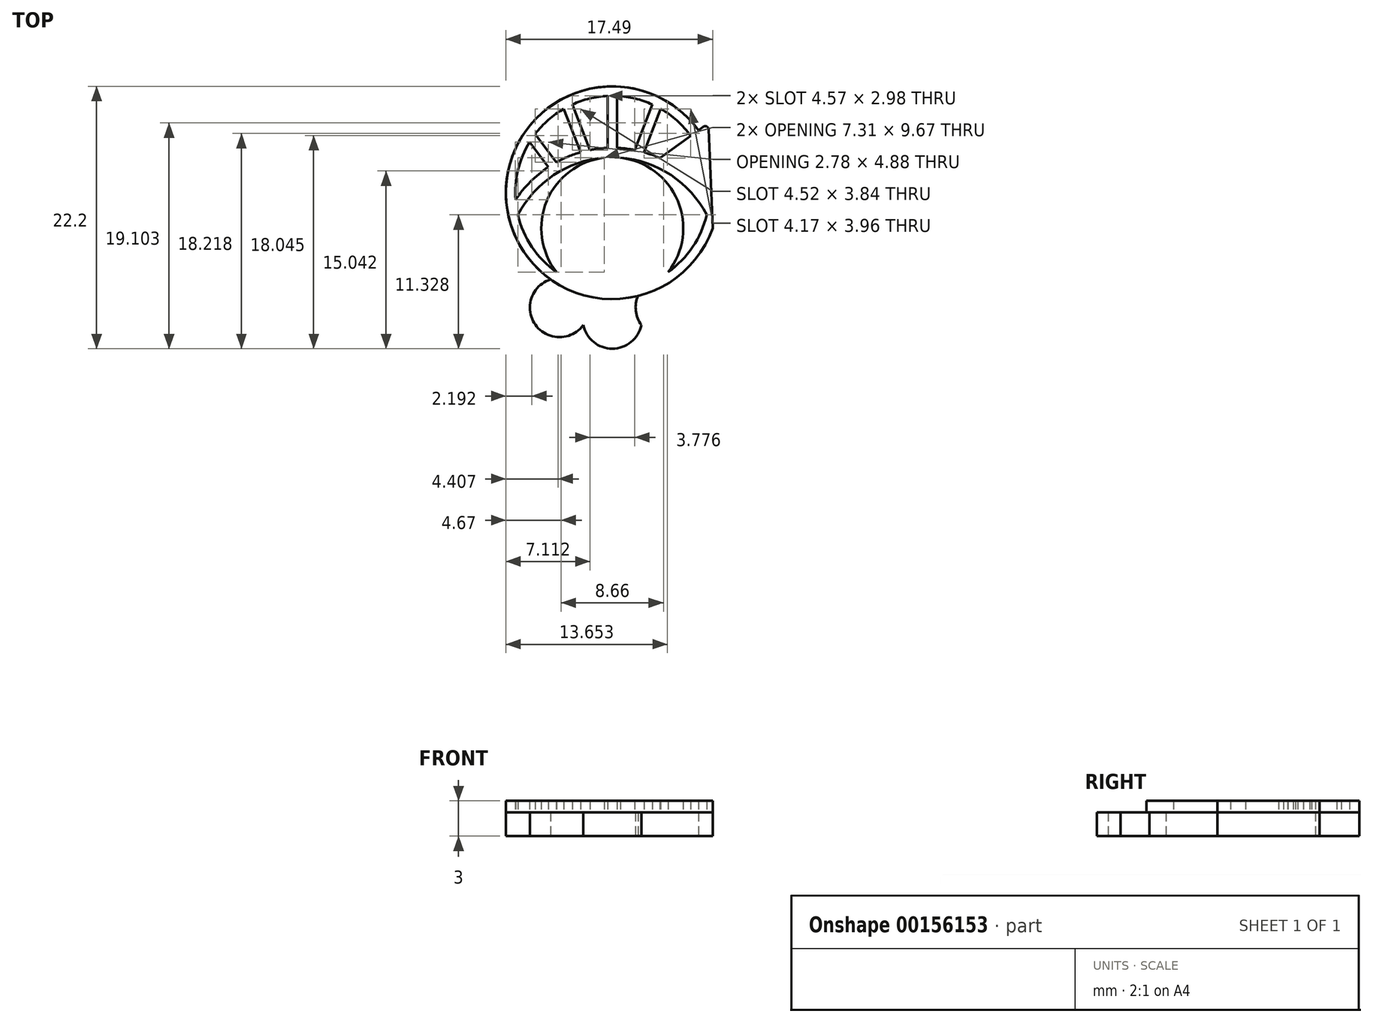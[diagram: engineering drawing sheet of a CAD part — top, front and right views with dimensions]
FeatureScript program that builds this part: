
annotation { "Feature Type Name" : "Feature", "Feature Type Description" : "" }
export const myFeature = defineFeature(function(context is Context, id is Id, definition is map)
    precondition{}
    {
        {
            var Q0;
            Q0=qCreatedBy(makeId("Top.planeOp"),FACE);
            var sketch = newSketch(context, id + "F0", { "sketchPlane" : qUnion([Q0])});
            skCircle(sketch, "E0", {"center": v(0, 0) * mm, "radius": 9 * mm});
            skLineSegment(sketch, "E1", {"start": v(0, -9) * mm, "end": v(0, -3) * mm, "construction": true});
            skLineSegment(sketch, "E2", {"start": v(-11.27, -3) * mm, "end": v(11.18, -3) * mm, "construction": true});
            skLineSegment(sketch, "E3", {"start": v(8.14, 5.36) * mm, "end": v(8.49, -3) * mm});
            skLineSegment(sketch, "E4", {"start": v(7.69, 5.58) * mm, "end": v(4.03, 2.93) * mm});
            skPoint(sketch, "E5.visualSharp", {"position": v(8.12, 5.9) * mm});
            skArc(sketch, "E5.filletArc", {"start": v(8.14, 5.36) * mm, "mid": v(7.98, 5.6) * mm, "end": v(7.69, 5.58) * mm});
            skCircle(sketch, "E6.0", {"center": v(0, 0) * mm, "radius": 8.2 * mm});
            skLineSegment(sketch, "E7", {"start": v(-7.53, 0.27) * mm, "end": v(-8.15, 0.95) * mm});
            skLineSegment(sketch, "E8", {"start": v(-7, 0.87) * mm, "end": v(-7.97, 1.94) * mm});
            skLineSegment(sketch, "E9", {"start": v(-5.42, 2.17) * mm, "end": v(-7, 4.28) * mm});
            skLineSegment(sketch, "E10", {"start": v(-4.73, 2.58) * mm, "end": v(-6.51, 4.98) * mm});
            skLineSegment(sketch, "E11", {"start": v(-2.67, 3.43) * mm, "end": v(-4.1, 7.1) * mm});
            skLineSegment(sketch, "E12", {"start": v(-1.89, 3.62) * mm, "end": v(-3.38, 7.47) * mm});
            skLineSegment(sketch, "E13", {"start": v(-0.4, 8.2) * mm, "end": v(-0.4, 3.8) * mm});
            skLineSegment(sketch, "E14", {"start": v(0.4, 8.2) * mm, "end": v(0.4, 3.8) * mm});
            skLineSegment(sketch, "E15", {"start": v(1.89, 3.62) * mm, "end": v(3.38, 7.47) * mm});
            skLineSegment(sketch, "E16", {"start": v(2.67, 3.43) * mm, "end": v(4.1, 7.1) * mm});
            skArc(sketch, "E17", {"start": v(8.18, -0.6) * mm, "mid": v(0, 3.8) * mm, "end": v(-8.18, -0.6) * mm});
            skArc(sketch, "E18", {"start": v(7.98, -1.87) * mm, "mid": v(0, 2.99) * mm, "end": v(-7.98, -1.87) * mm});
            skArc(sketch, "E19", {"start": v(-5.22, -7.33) * mm, "mid": v(-6.5, -11.18) * mm, "end": v(-2.45, -11.2) * mm});
            skArc(sketch, "E20", {"start": v(-2.02, -9.23) * mm, "mid": v(-2.08, -8.98) * mm, "end": v(-2.17, -8.73) * mm});
            skArc(sketch, "E21", {"start": v(-2.45, -11.2) * mm, "mid": v(-2.03, -10.26) * mm, "end": v(-2.02, -9.23) * mm});
            skArc(sketch, "E22", {"start": v(4.72, -6.7) * mm, "mid": v(5.48, -0.56) * mm, "end": v(0.4, 2.99) * mm});
            skArc(sketch, "E23", {"start": v(-1.67, -8.84) * mm, "mid": v(0, -13.2) * mm, "end": v(1.67, -8.84) * mm});
            skArc(sketch, "E24", {"start": v(5.22, -7.33) * mm, "mid": v(5.52, -12) * mm, "end": v(2.17, -8.73) * mm});
            skArc(sketch, "E25", {"start": v(-0.68, 2.96) * mm, "mid": v(-5.54, -0.69) * mm, "end": v(-4.72, -6.7) * mm});
            skSolve(sketch);
        }
        {
            var Q0;
            {var subQ0=sQuery(id+"F0.wireOp",EDGE,"E9");Q0=makeQuery(id+"F0.imprint","IMPRINT",FACE,{"disambiguationData":[TD([[makeQuery(id+"F0.imprint","IMPRINT",EDGE,{"derivedFrom":subQ0}),-1.0]])]});}
            var Q1;
            {var subQ0=sQuery(id+"F0.wireOp",EDGE,"E17");var subQ6=sQuery(id+"F0.wireOp",EDGE,"E6.0");var subQ14=makeQuery(id+"F0.imprint","INTERSECT",VERTEX,{"disambiguationData":[OD(1.0)],"derivedFrom":[subQ6,subQ0]});Q1=makeQuery(id+"F0.imprint","IMPRINT",FACE,{"disambiguationData":[TD([[makeQuery(id+"F0.imprint","IMPRINT",EDGE,{"disambiguationData":[TD([[subQ14,-1.0]])],"derivedFrom":subQ6}),1.0]])]});}
            var Q2;
            {var subQ0=sQuery(id+"F0.wireOp",EDGE,"E12");Q2=makeQuery(id+"F0.imprint","IMPRINT",FACE,{"disambiguationData":[TD([[makeQuery(id+"F0.imprint","IMPRINT",EDGE,{"derivedFrom":subQ0}),-1.0]])]});}
            var Q3;
            {var subQ0=sQuery(id+"F0.wireOp",EDGE,"E24");var subQ1=sQuery(id+"F0.wireOp",EDGE,"E0");var subQ2=makeQuery(id+"F0.imprint","INTERSECT",VERTEX,{"disambiguationData":[OD(0.0)],"derivedFrom":[subQ1,subQ0]});Q3=makeQuery(id+"F0.imprint","IMPRINT",FACE,{"disambiguationData":[TD([[makeQuery(id+"F0.imprint","IMPRINT",EDGE,{"disambiguationData":[TD([[subQ2,1.0]])],"derivedFrom":subQ1}),-1.0]])]});}
            var Q4;
            {var subQ0=sQuery(id+"F0.wireOp",EDGE,"E22");var subQ1=sQuery(id+"F0.wireOp",EDGE,"E6.0");var subQ2=makeQuery(id+"F0.imprint","INTERSECT",VERTEX,{"disambiguationData":[OD(0.0)],"derivedFrom":[subQ1,subQ0]});Q4=makeQuery(id+"F0.imprint","IMPRINT",FACE,{"disambiguationData":[TD([[makeQuery(id+"F0.imprint","IMPRINT",EDGE,{"disambiguationData":[TD([[subQ2,1.0]])],"derivedFrom":subQ1}),1.0]])]});}
            var Q5;
            {var subQ5=sQuery(id+"F0.wireOp",EDGE,"E16");Q5=makeQuery(id+"F0.imprint","IMPRINT",FACE,{"disambiguationData":[TD([[makeQuery(id+"F0.imprint","IMPRINT",EDGE,{"derivedFrom":subQ5}),-1.0]])]});}
            var Q6;
            {var subQ0=sQuery(id+"F0.wireOp",EDGE,"E3");var subQ1=sQuery(id+"F0.wireOp",EDGE,"E0");var subQ2=makeQuery(id+"F0.imprint","INTERSECT",VERTEX,{"disambiguationData":[OD(0.0)],"derivedFrom":[subQ1,subQ0]});Q6=makeQuery(id+"F0.imprint","IMPRINT",FACE,{"disambiguationData":[TD([[makeQuery(id+"F0.imprint","IMPRINT",EDGE,{"disambiguationData":[TD([[subQ2,-1.0]])],"derivedFrom":subQ1}),1.0]])]});}
            var Q7;
            {var subQ0=sQuery(id+"F0.wireOp",EDGE,"E11");Q7=makeQuery(id+"F0.imprint","IMPRINT",FACE,{"disambiguationData":[TD([[makeQuery(id+"F0.imprint","IMPRINT",EDGE,{"derivedFrom":subQ0}),-1.0]])]});}
            var Q8;
            {var subQ0=sQuery(id+"F0.wireOp",EDGE,"E7");Q8=makeQuery(id+"F0.imprint","IMPRINT",FACE,{"disambiguationData":[TD([[makeQuery(id+"F0.imprint","IMPRINT",EDGE,{"derivedFrom":subQ0}),-1.0]])]});}
            var Q9;
            {var subQ0=sQuery(id+"F0.wireOp",EDGE,"E19");Q9=makeQuery(id+"F0.imprint","IMPRINT",FACE,{"disambiguationData":[TD([[makeQuery(id+"F0.imprint","IMPRINT",EDGE,{"derivedFrom":subQ0}),1.0]])]});}
            var Q10;
            {var subQ0=sQuery(id+"F0.wireOp",EDGE,"E10");Q10=makeQuery(id+"F0.imprint","IMPRINT",FACE,{"disambiguationData":[TD([[makeQuery(id+"F0.imprint","IMPRINT",EDGE,{"derivedFrom":subQ0}),-1.0]])]});}
            var Q11;
            {var subQ0=sQuery(id+"F0.wireOp",EDGE,"E18");var subQ1=sQuery(id+"F0.wireOp",EDGE,"E6.0");var subQ2=makeQuery(id+"F0.imprint","INTERSECT",VERTEX,{"disambiguationData":[OD(1.0)],"derivedFrom":[subQ1,subQ0]});Q11=makeQuery(id+"F0.imprint","IMPRINT",FACE,{"disambiguationData":[TD([[makeQuery(id+"F0.imprint","IMPRINT",EDGE,{"disambiguationData":[TD([[subQ2,-1.0]])],"derivedFrom":subQ1}),1.0]])]});}
            var Q12;
            {var subQ0=sQuery(id+"F0.wireOp",EDGE,"E24");var subQ1=sQuery(id+"F0.wireOp",EDGE,"E23");var subQ2=makeQuery(id+"F0.imprint","INTERSECT",VERTEX,{"disambiguationData":[OD(0.0)],"derivedFrom":[subQ1,subQ0]});Q12=makeQuery(id+"F0.imprint","IMPRINT",FACE,{"disambiguationData":[TD([[makeQuery(id+"F0.imprint","IMPRINT",EDGE,{"disambiguationData":[TD([[subQ2,-1.0]])],"derivedFrom":subQ1}),1.0]])]});}
            var Q13;
            {var subQ0=sQuery(id+"F0.wireOp",EDGE,"E8");Q13=makeQuery(id+"F0.imprint","IMPRINT",FACE,{"disambiguationData":[TD([[makeQuery(id+"F0.imprint","IMPRINT",EDGE,{"derivedFrom":subQ0}),-1.0]])]});}
            var Q14;
            {var subQ14=sQuery(id+"F0.wireOp",EDGE,"E0");var subQ21=sQuery(id+"F0.wireOp",EDGE,"E4");var subQ27=makeQuery(id+"F0.imprint","INTERSECT",VERTEX,{"derivedFrom":[subQ14,subQ21]});Q14=makeQuery(id+"F0.imprint","IMPRINT",FACE,{"disambiguationData":[TD([[makeQuery(id+"F0.imprint","IMPRINT",EDGE,{"disambiguationData":[TD([[subQ27,1.0]])],"derivedFrom":subQ14}),1.0]])]});}
            var Q15;
            {var subQ0=sQuery(id+"F0.wireOp",EDGE,"E13");Q15=makeQuery(id+"F0.imprint","IMPRINT",FACE,{"disambiguationData":[TD([[makeQuery(id+"F0.imprint","IMPRINT",EDGE,{"derivedFrom":subQ0}),1.0]])]});}
            var Q16;
            {var subQ0=sQuery(id+"F0.wireOp",EDGE,"E7");Q16=makeQuery(id+"F0.imprint","IMPRINT",FACE,{"disambiguationData":[TD([[makeQuery(id+"F0.imprint","IMPRINT",EDGE,{"derivedFrom":subQ0}),1.0]])]});}
            var Q17;
            {var subQ0=sQuery(id+"F0.wireOp",EDGE,"E15");Q17=makeQuery(id+"F0.imprint","IMPRINT",FACE,{"disambiguationData":[TD([[makeQuery(id+"F0.imprint","IMPRINT",EDGE,{"derivedFrom":subQ0}),-1.0]])]});}
            var Q18;
            {var subQ0=sQuery(id+"F0.wireOp",EDGE,"E14");Q18=makeQuery(id+"F0.imprint","IMPRINT",FACE,{"disambiguationData":[TD([[makeQuery(id+"F0.imprint","IMPRINT",EDGE,{"derivedFrom":subQ0}),1.0]])]});}
            var Q19;
            {var subQ0=sQuery(id+"F0.wireOp",EDGE,"E21");Q19=makeQuery(id+"F0.imprint","IMPRINT",FACE,{"disambiguationData":[TD([[makeQuery(id+"F0.imprint","IMPRINT",EDGE,{"derivedFrom":subQ0}),1.0]])]});}
            var Q20;
            {var subQ0=sQuery(id+"F0.wireOp",EDGE,"E17");var subQ1=sQuery(id+"F0.wireOp",EDGE,"E4");var subQ2=makeQuery(id+"F0.imprint","INTERSECT",VERTEX,{"derivedFrom":[subQ1,subQ0]});Q20=makeQuery(id+"F0.imprint","IMPRINT",FACE,{"disambiguationData":[TD([[makeQuery(id+"F0.imprint","IMPRINT",EDGE,{"disambiguationData":[TD([[subQ2,1.0]])],"derivedFrom":subQ1}),1.0]])]});}
            var Q21;
            {var subQ1=sQuery(id+"F0.wireOp",EDGE,"E21");Q21=makeQuery(id+"F0.imprint","IMPRINT",FACE,{"disambiguationData":[TD([[makeQuery(id+"F0.imprint","IMPRINT",EDGE,{"derivedFrom":subQ1}),-1.0]])]});}
            var Q22;
            {var subQ0=sQuery(id+"F0.wireOp",EDGE,"E18");var subQ1=sQuery(id+"F0.wireOp",EDGE,"E6.0");var subQ2=makeQuery(id+"F0.imprint","INTERSECT",VERTEX,{"disambiguationData":[OD(0.0)],"derivedFrom":[subQ1,subQ0]});Q22=makeQuery(id+"F0.imprint","IMPRINT",FACE,{"disambiguationData":[TD([[makeQuery(id+"F0.imprint","IMPRINT",EDGE,{"disambiguationData":[TD([[subQ2,1.0]])],"derivedFrom":subQ1}),1.0]])]});}
            var Q23;
            {var subQ5=sQuery(id+"F0.wireOp",EDGE,"E5.filletArc");Q23=makeQuery(id+"F0.imprint","IMPRINT",FACE,{"disambiguationData":[TD([[makeQuery(id+"F0.imprint","IMPRINT",EDGE,{"derivedFrom":subQ5}),1.0]])]});}
            var Q24;
            {var subQ0=sQuery(id+"F0.wireOp",EDGE,"E20");Q24=makeQuery(id+"F0.imprint","IMPRINT",FACE,{"disambiguationData":[TD([[makeQuery(id+"F0.imprint","IMPRINT",EDGE,{"derivedFrom":subQ0}),-1.0]])]});}
            var Q25;
            {var subQ0=sQuery(id+"F0.wireOp",EDGE,"E23");var subQ1=sQuery(id+"F0.wireOp",EDGE,"E0");var subQ2=makeQuery(id+"F0.imprint","INTERSECT",VERTEX,{"disambiguationData":[OD(1.0)],"derivedFrom":[subQ1,subQ0]});Q25=makeQuery(id+"F0.imprint","IMPRINT",FACE,{"disambiguationData":[TD([[makeQuery(id+"F0.imprint","IMPRINT",EDGE,{"disambiguationData":[TD([[subQ2,-1.0]])],"derivedFrom":subQ1}),-1.0]])]});}
            extrude(context, id + "F1", {"entities" : qUnion([Q0, Q1, Q2, Q3, Q4, Q5, Q6, Q7, Q8, Q9, Q10, Q11, Q12, Q13, Q14, Q15, Q16, Q17, Q18, Q19, Q20, Q21, Q22, Q23, Q24, Q25]), "depth" : 2 * mm});
        }
        {
            var Q0;
            {var subQ0=sQuery(id+"F0.wireOp",EDGE,"E9");Q0=makeQuery(id+"F0.imprint","IMPRINT",FACE,{"disambiguationData":[TD([[makeQuery(id+"F0.imprint","IMPRINT",EDGE,{"derivedFrom":subQ0}),-1.0]])]});}
            var Q1;
            {var subQ0=sQuery(id+"F0.wireOp",EDGE,"E11");Q1=makeQuery(id+"F0.imprint","IMPRINT",FACE,{"disambiguationData":[TD([[makeQuery(id+"F0.imprint","IMPRINT",EDGE,{"derivedFrom":subQ0}),-1.0]])]});}
            var Q2;
            {var subQ0=sQuery(id+"F0.wireOp",EDGE,"E13");Q2=makeQuery(id+"F0.imprint","IMPRINT",FACE,{"disambiguationData":[TD([[makeQuery(id+"F0.imprint","IMPRINT",EDGE,{"derivedFrom":subQ0}),1.0]])]});}
            var Q3;
            {var subQ0=sQuery(id+"F0.wireOp",EDGE,"E15");Q3=makeQuery(id+"F0.imprint","IMPRINT",FACE,{"disambiguationData":[TD([[makeQuery(id+"F0.imprint","IMPRINT",EDGE,{"derivedFrom":subQ0}),-1.0]])]});}
            var Q4;
            {var subQ0=sQuery(id+"F0.wireOp",EDGE,"E17");var subQ1=sQuery(id+"F0.wireOp",EDGE,"E4");var subQ2=makeQuery(id+"F0.imprint","INTERSECT",VERTEX,{"derivedFrom":[subQ1,subQ0]});Q4=makeQuery(id+"F0.imprint","IMPRINT",FACE,{"disambiguationData":[TD([[makeQuery(id+"F0.imprint","IMPRINT",EDGE,{"disambiguationData":[TD([[subQ2,1.0]])],"derivedFrom":subQ1}),1.0]])]});}
            var Q5;
            {var subQ14=sQuery(id+"F0.wireOp",EDGE,"E0");var subQ21=sQuery(id+"F0.wireOp",EDGE,"E4");var subQ27=makeQuery(id+"F0.imprint","INTERSECT",VERTEX,{"derivedFrom":[subQ14,subQ21]});Q5=makeQuery(id+"F0.imprint","IMPRINT",FACE,{"disambiguationData":[TD([[makeQuery(id+"F0.imprint","IMPRINT",EDGE,{"disambiguationData":[TD([[subQ27,1.0]])],"derivedFrom":subQ14}),1.0]])]});}
            var Q6;
            {var subQ5=sQuery(id+"F0.wireOp",EDGE,"E5.filletArc");Q6=makeQuery(id+"F0.imprint","IMPRINT",FACE,{"disambiguationData":[TD([[makeQuery(id+"F0.imprint","IMPRINT",EDGE,{"derivedFrom":subQ5}),1.0]])]});}
            var Q7;
            {var subQ0=sQuery(id+"F0.wireOp",EDGE,"E3");var subQ1=sQuery(id+"F0.wireOp",EDGE,"E0");var subQ2=makeQuery(id+"F0.imprint","INTERSECT",VERTEX,{"disambiguationData":[OD(0.0)],"derivedFrom":[subQ1,subQ0]});Q7=makeQuery(id+"F0.imprint","IMPRINT",FACE,{"disambiguationData":[TD([[makeQuery(id+"F0.imprint","IMPRINT",EDGE,{"disambiguationData":[TD([[subQ2,-1.0]])],"derivedFrom":subQ1}),1.0]])]});}
            var Q8;
            {var subQ0=sQuery(id+"F0.wireOp",EDGE,"E17");var subQ6=sQuery(id+"F0.wireOp",EDGE,"E6.0");var subQ14=makeQuery(id+"F0.imprint","INTERSECT",VERTEX,{"disambiguationData":[OD(1.0)],"derivedFrom":[subQ6,subQ0]});Q8=makeQuery(id+"F0.imprint","IMPRINT",FACE,{"disambiguationData":[TD([[makeQuery(id+"F0.imprint","IMPRINT",EDGE,{"disambiguationData":[TD([[subQ14,-1.0]])],"derivedFrom":subQ6}),1.0]])]});}
            var Q9;
            {var subQ3=sQuery(id+"F0.wireOp",EDGE,"E25");Q9=makeQuery(id+"F0.imprint","IMPRINT",FACE,{"disambiguationData":[TD([[makeQuery(id+"F0.imprint","IMPRINT",EDGE,{"derivedFrom":subQ3}),1.0]])]});}
            extrude(context, id + "F2", {"entities" : qUnion([Q0, Q1, Q2, Q3, Q4, Q5, Q6, Q7, Q8, Q9]), "depth" : 1 * mm});
        }
        {
            var Q0;
            Q0=makeQuery(id+"F2.opExtrude","SWEPT_BODY",BODY,{"disambiguationData":[OSD([sQuery(id+"F0.wireOp",EDGE,"E0"),sQuery(id+"F0.wireOp",EDGE,"E3"),sQuery(id+"F0.wireOp",EDGE,"E4"),sQuery(id+"F0.wireOp",EDGE,"E5.filletArc"),sQuery(id+"F0.wireOp",EDGE,"E6.0"),sQuery(id+"F0.wireOp",EDGE,"E9"),sQuery(id+"F0.wireOp",EDGE,"E10"),sQuery(id+"F0.wireOp",EDGE,"E11"),sQuery(id+"F0.wireOp",EDGE,"E12"),sQuery(id+"F0.wireOp",EDGE,"E13"),sQuery(id+"F0.wireOp",EDGE,"E14"),sQuery(id+"F0.wireOp",EDGE,"E15"),sQuery(id+"F0.wireOp",EDGE,"E16"),sQuery(id+"F0.wireOp",EDGE,"E17"),sQuery(id+"F0.wireOp",EDGE,"E18"),sQuery(id+"F0.wireOp",EDGE,"E22"),sQuery(id+"F0.wireOp",EDGE,"E25")])]});
            transform(context, id + "F3", {"entities" : qUnion([Q0]), "transformType" : TransformType.TRANSLATION_3D, "dx" : 0 * mm, "dy" : 0 * mm, "dz" : 2 * mm, "makeCopy" : false});
        }
    });
